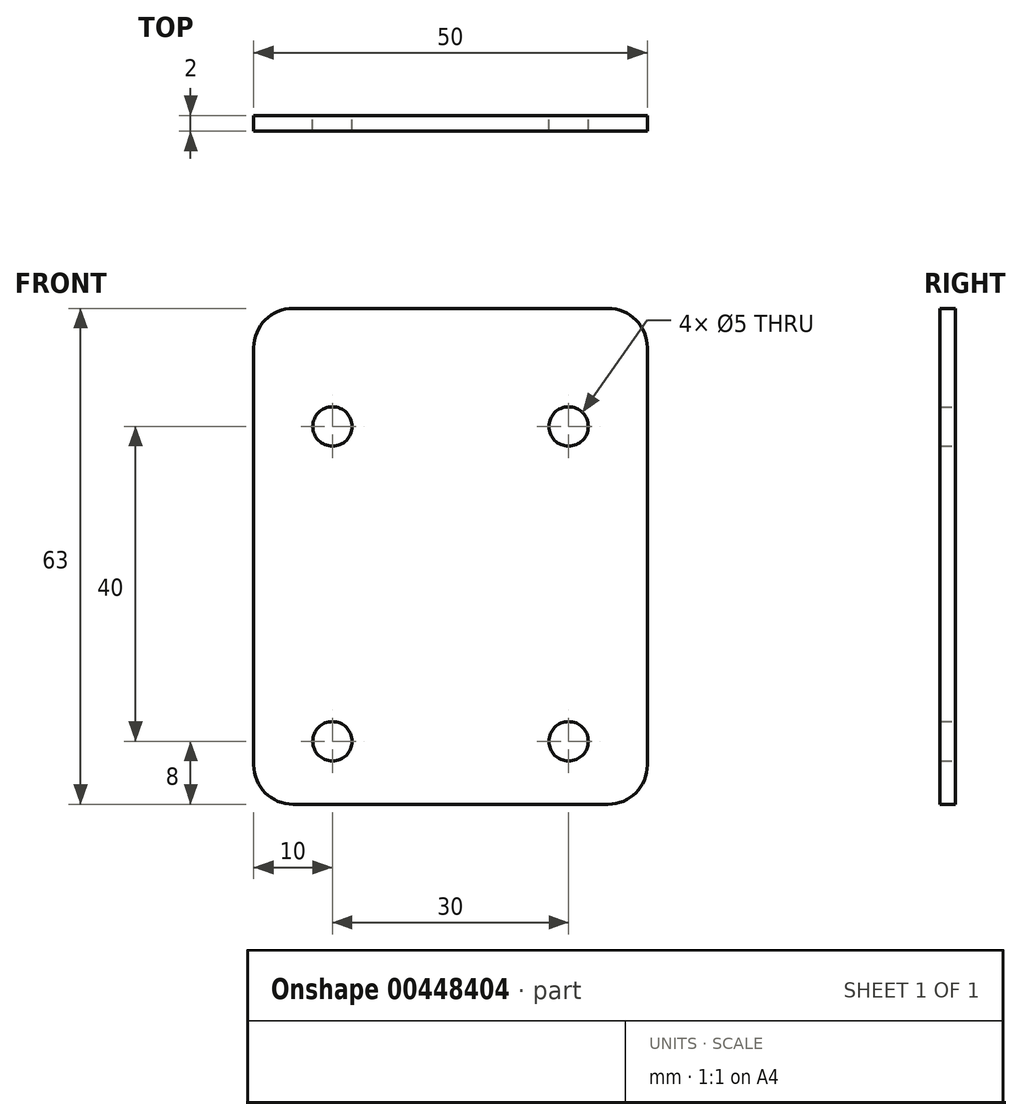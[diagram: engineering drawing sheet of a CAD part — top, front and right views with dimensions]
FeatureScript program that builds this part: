
annotation { "Feature Type Name" : "Feature", "Feature Type Description" : "" }
export const myFeature = defineFeature(function(context is Context, id is Id, definition is map)
    precondition{}
    {
        {
            var Q0;
            Q0=qCreatedBy(makeId("Front.planeOp"),FACE);
            var sketch = newSketch(context, id + "F0", { "sketchPlane" : qUnion([Q0])});
            skArc(sketch, "E0", {"start": v(-418, 418) * mm, "mid": v(-295.57, 122.43) * mm, "end": v(0, 0) * mm, "construction": true});
            skLineSegment(sketch, "E1", {"start": v(0, 0) * mm, "end": v(0, 50.54) * mm});
            skLineSegment(sketch, "E2.trimOffspring", {"start": v(0, 0) * mm, "end": v(0, 418) * mm, "construction": true});
            skArc(sketch, "E3", {"start": v(-18.91, 70.51) * mm, "mid": v(-5.48, 64.3) * mm, "end": v(0, 50.54) * mm, "construction": true});
            skLineSegment(sketch, "E4", {"start": v(0, 418) * mm, "end": v(-418, 418) * mm, "construction": true});
            skArc(sketch, "E5", {"start": v(-348, 418) * mm, "mid": v(-246.07, 171.93) * mm, "end": v(0, 70) * mm, "construction": true});
            skArc(sketch, "E6", {"start": v(-403, 418) * mm, "mid": v(-284.96, 133.04) * mm, "end": v(0, 15) * mm, "construction": true});
            skLineSegment(sketch, "E7", {"start": v(0, 418) * mm, "end": v(-22.72, 0.62) * mm, "construction": true});
            skCircle(sketch, "E8", {"center": v(-15, 55) * mm, "radius": 2.5 * mm});
            skLineSegment(sketch, "E9.bottom", {"start": v(0, 70) * mm, "end": v(-25, 70) * mm});
            skLineSegment(sketch, "E9.top", {"start": v(0, 7) * mm, "end": v(-25, 7) * mm});
            skLineSegment(sketch, "E9.left", {"start": v(0, 70) * mm, "end": v(0, 7) * mm});
            skLineSegment(sketch, "E9.right", {"start": v(-25, 70) * mm, "end": v(-25, 7) * mm});
            skLineSegment(sketch, "E10.MirrorCS", {"start": v(0, 70) * mm, "end": v(25, 70) * mm});
            skLineSegment(sketch, "E11.MirrorCS", {"start": v(25, 70) * mm, "end": v(25, 7) * mm});
            skLineSegment(sketch, "E12.MirrorCS", {"start": v(0, 7) * mm, "end": v(25, 7) * mm});
            skCircle(sketch, "E13.MirrorC", {"center": v(15, 55) * mm, "radius": 2.5 * mm});
            skLineSegment(sketch, "E14.MirrorCS", {"start": v(0, 418) * mm, "end": v(22.72, 0.62) * mm, "construction": true});
            skArc(sketch, "E15.MirrorCS", {"start": v(18.91, 70.51) * mm, "mid": v(5.48, 64.3) * mm, "end": v(0, 50.54) * mm, "construction": true});
            skLineSegment(sketch, "E16", {"start": v(0, 0) * mm, "end": v(-82.21, 0) * mm, "construction": true});
            skLineSegment(sketch, "E17", {"start": v(-15, 0) * mm, "end": v(-15, 65.81) * mm, "construction": true});
            skCircle(sketch, "E18", {"center": v(-15, 15) * mm, "radius": 2.5 * mm});
            skPoint(sketch, "E19", {"position": v(-12.5, 70) * mm});
            skCircle(sketch, "E20.MirrorC", {"center": v(15, 15) * mm, "radius": 2.5 * mm});
            skLineSegment(sketch, "E21.MirrorCS", {"start": v(15, 0) * mm, "end": v(15, 65.81) * mm, "construction": true});
            skSolve(sketch);
        }
        {
            var Q0;
            Q0=qSketchRegion(id+"F0",true);
            extrude(context, id + "F1", {"entities" : qUnion([Q0]), "depth" : 2 * mm});
        }
        {
            var Q0;
            Q0=makeQuery(id+"F1.opExtrude","SWEPT_EDGE",EDGE,{"disambiguationData":[OSD([sQuery(id+"F0.wireOp",EDGE,"E9.bottom"),sQuery(id+"F0.wireOp",EDGE,"E9.right")])]});
            var Q1;
            Q1=makeQuery(id+"F1.opExtrude","SWEPT_EDGE",EDGE,{"disambiguationData":[OSD([sQuery(id+"F0.wireOp",EDGE,"E10.MirrorCS"),sQuery(id+"F0.wireOp",EDGE,"E11.MirrorCS")])]});
            var Q2;
            Q2=makeQuery(id+"F1.opExtrude","SWEPT_EDGE",EDGE,{"disambiguationData":[OSD([sQuery(id+"F0.wireOp",EDGE,"E9.top"),sQuery(id+"F0.wireOp",EDGE,"E9.right")])]});
            var Q3;
            Q3=makeQuery(id+"F1.opExtrude","SWEPT_EDGE",EDGE,{"disambiguationData":[OSD([sQuery(id+"F0.wireOp",EDGE,"E11.MirrorCS"),sQuery(id+"F0.wireOp",EDGE,"E12.MirrorCS")])]});
            fillet(context, id + "F2", {"entities" : qUnion([Q0, Q1, Q2, Q3]), "radius" : 5 * mm, "tangentPropagation" : true, "allowEdgeOverflow" : false});
        }
    });
